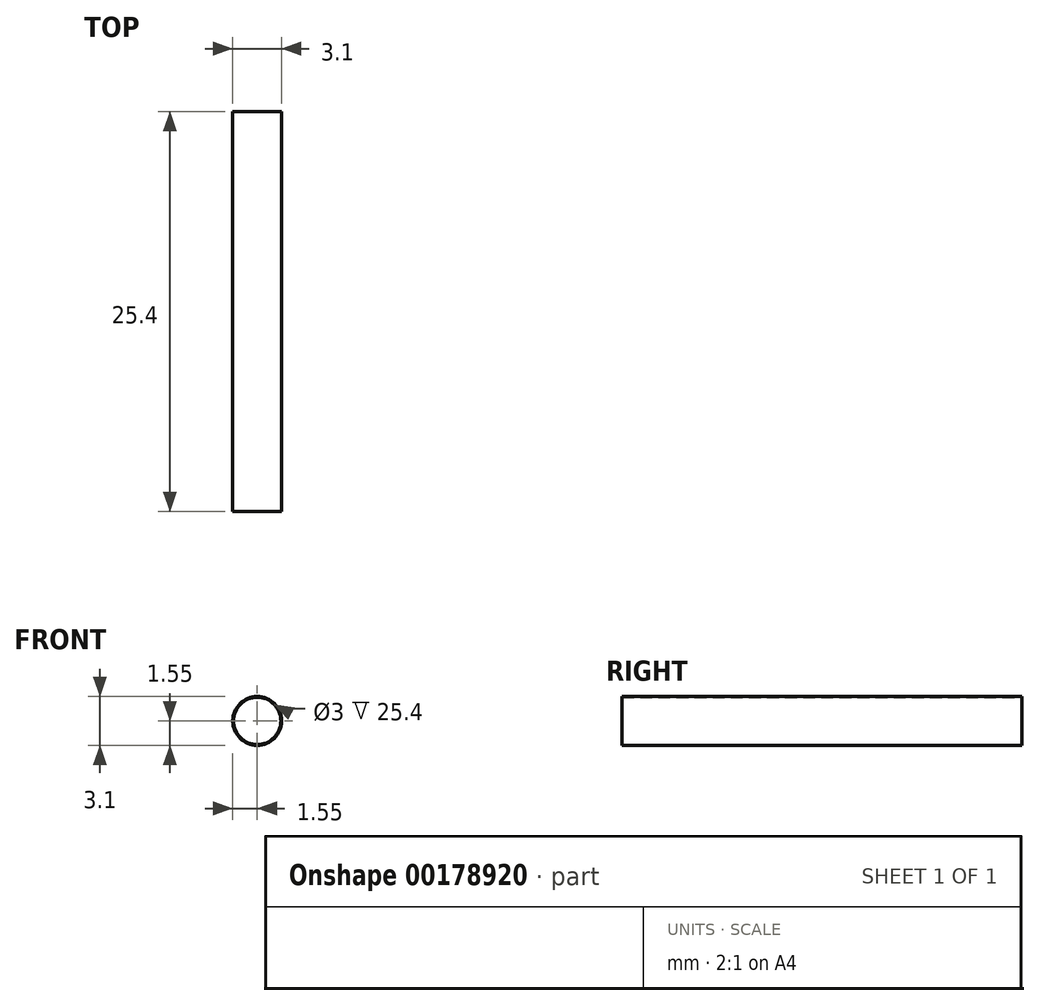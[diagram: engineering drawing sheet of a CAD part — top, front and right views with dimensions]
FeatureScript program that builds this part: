
annotation { "Feature Type Name" : "Feature", "Feature Type Description" : "" }
export const myFeature = defineFeature(function(context is Context, id is Id, definition is map)
    precondition{}
    {
        {
            var Q0;
            Q0=qCreatedBy(makeId("Front.planeOp"),FACE);
            var sketch = newSketch(context, id + "F0", { "sketchPlane" : qUnion([Q0])});
            skCircle(sketch, "E0", {"center": v(0, 0) * mm, "radius": 1.55 * mm});
            skCircle(sketch, "E1", {"center": v(0, 0) * mm, "radius": 1.5 * mm});
            skSolve(sketch);
        }
        {
            var Q0;
            Q0=makeQuery(id+"F0.imprint","IMPRINT",FACE,{"disambiguationData":[TD([[makeQuery(id+"F0.imprint","IMPRINT",EDGE,{"derivedFrom":sQuery(id+"F0.wireOp",EDGE,"E0")}),1.0]])]});
            extrude(context, id + "F1", {"entities" : qUnion([Q0]), "depth" : 25.4 * mm});
        }
    });
